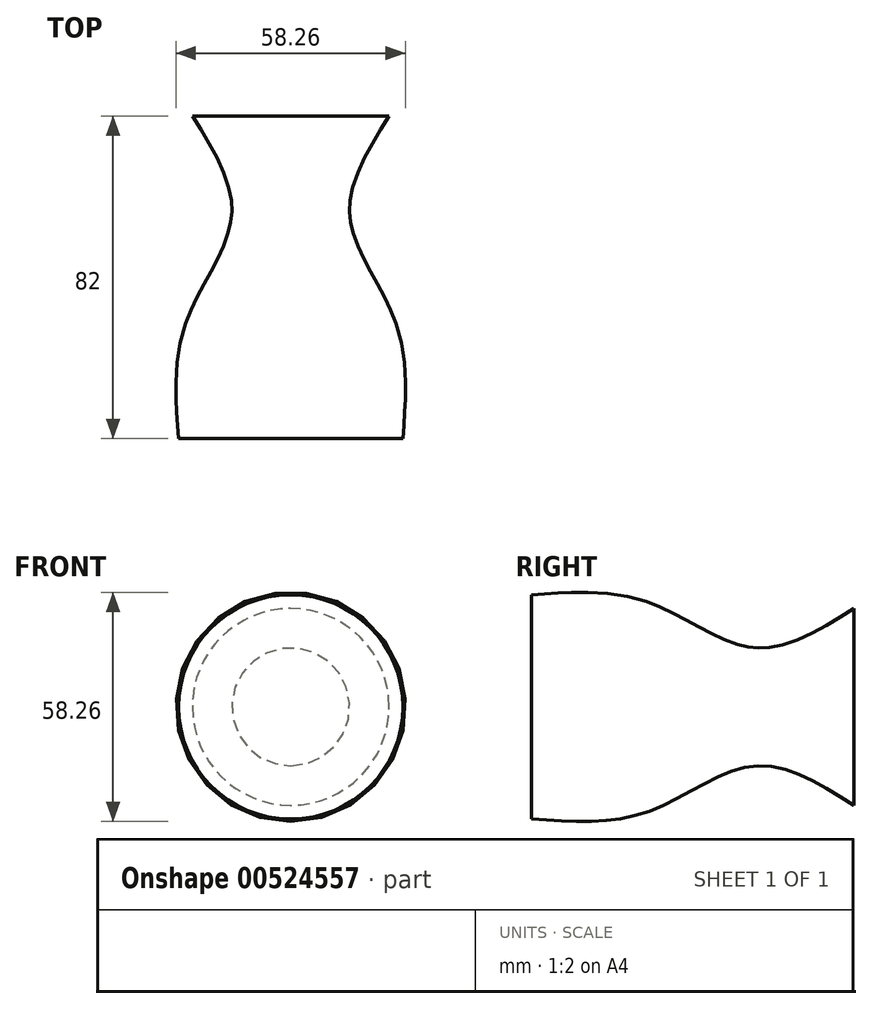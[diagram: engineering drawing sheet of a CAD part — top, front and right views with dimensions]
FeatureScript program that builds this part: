
annotation { "Feature Type Name" : "Feature", "Feature Type Description" : "" }
export const myFeature = defineFeature(function(context is Context, id is Id, definition is map)
    precondition{}
    {
        {
            var Q0;
            Q0=qCreatedBy(makeId("Front.planeOp"),FACE);
            var sketch = newSketch(context, id + "F0", { "sketchPlane" : qUnion([Q0])});
            skCircle(sketch, "E0", {"center": v(0, 0) * mm, "radius": 25 * mm});
            skSolve(sketch);
        }
        {
            var Q0;
            Q0=qCreatedBy(makeId("Front.planeOp"),FACE);
            cPlane(context, id + "F1", {"entities" : qUnion([Q0]), "cplaneType" : CPlaneType.OFFSET, "offset" : 25 * mm, "width" : 150 * mm, "height" : 150 * mm});
        }
        {
            var Q0;
            Q0=qCreatedBy(id+"F1.planeOp",FACE);
            var sketch = newSketch(context, id + "F2", { "sketchPlane" : qUnion([Q0])});
            skCircle(sketch, "E1", {"center": v(0, 0) * mm, "radius": 15 * mm});
            skSolve(sketch);
        }
        {
            var Q0;
            Q0=qCreatedBy(id+"F1.planeOp",FACE);
            cPlane(context, id + "F3", {"entities" : qUnion([Q0]), "cplaneType" : CPlaneType.OFFSET, "offset" : 27 * mm, "width" : 150 * mm, "height" : 150 * mm});
        }
        {
            var Q0;
            Q0=qCreatedBy(id+"F3.planeOp",FACE);
            var sketch = newSketch(context, id + "F4", { "sketchPlane" : qUnion([Q0])});
            skCircle(sketch, "E2", {"center": v(0, 0) * mm, "radius": 26.5 * mm});
            skSolve(sketch);
        }
        {
            var Q0;
            Q0=qCreatedBy(id+"F3.planeOp",FACE);
            cPlane(context, id + "F5", {"entities" : qUnion([Q0]), "cplaneType" : CPlaneType.OFFSET, "offset" : 30 * mm, "width" : 150 * mm, "height" : 150 * mm});
        }
        {
            var Q0;
            Q0=qCreatedBy(id+"F5.planeOp",FACE);
            var sketch = newSketch(context, id + "F6", { "sketchPlane" : qUnion([Q0])});
            skCircle(sketch, "E3", {"center": v(0, 0) * mm, "radius": 28.5 * mm});
            skSolve(sketch);
        }
        {
            var Q0;
            Q0=qCreatedBy(makeId("Right.planeOp"),FACE);
            var sketch = newSketch(context, id + "F7", { "sketchPlane" : qUnion([Q0])});
            skArc(sketch, "E4", {"start": v(-82, 26.88) * mm, "mid": v(-67.06, 25.47) * mm, "end": v(-52.07, 26.03) * mm});
            skSolve(sketch);
        }
        {
            var Q0;
            Q0=sQuery(id+"F7.wireOp",EDGE,"E4");
            var Q1;
            Q1=makeQuery(id+"F0.imprint","IMPRINT",FACE,{"disambiguationData":[TD([[makeQuery(id+"F0.imprint","IMPRINT",EDGE,{"derivedFrom":sQuery(id+"F0.wireOp",EDGE,"E0")}),1.0]])]});
            var Q2;
            Q2=makeQuery(id+"F2.imprint","IMPRINT",FACE,{"disambiguationData":[TD([[makeQuery(id+"F2.imprint","IMPRINT",EDGE,{"derivedFrom":sQuery(id+"F2.wireOp",EDGE,"E1")}),1.0]])]});
            var Q3;
            Q3=makeQuery(id+"F4.imprint","IMPRINT",FACE,{"disambiguationData":[TD([[makeQuery(id+"F4.imprint","IMPRINT",EDGE,{"derivedFrom":sQuery(id+"F4.wireOp",EDGE,"E2")}),1.0]])]});
            var Q4;
            Q4=makeQuery(id+"F6.imprint","IMPRINT",FACE,{"disambiguationData":[TD([[makeQuery(id+"F6.imprint","IMPRINT",EDGE,{"derivedFrom":sQuery(id+"F6.wireOp",EDGE,"E3")}),1.0]])]});
            loft(context, id + "F8", {"spine" : qUnion([Q0]), "sheetProfilesArray" : [{ "sheetProfileEntities" : qUnion([Q1]) }, { "sheetProfileEntities" : qUnion([Q2]) }, { "sheetProfileEntities" : qUnion([Q3]) }, { "sheetProfileEntities" : qUnion([Q4]) }]});
        }
    });
